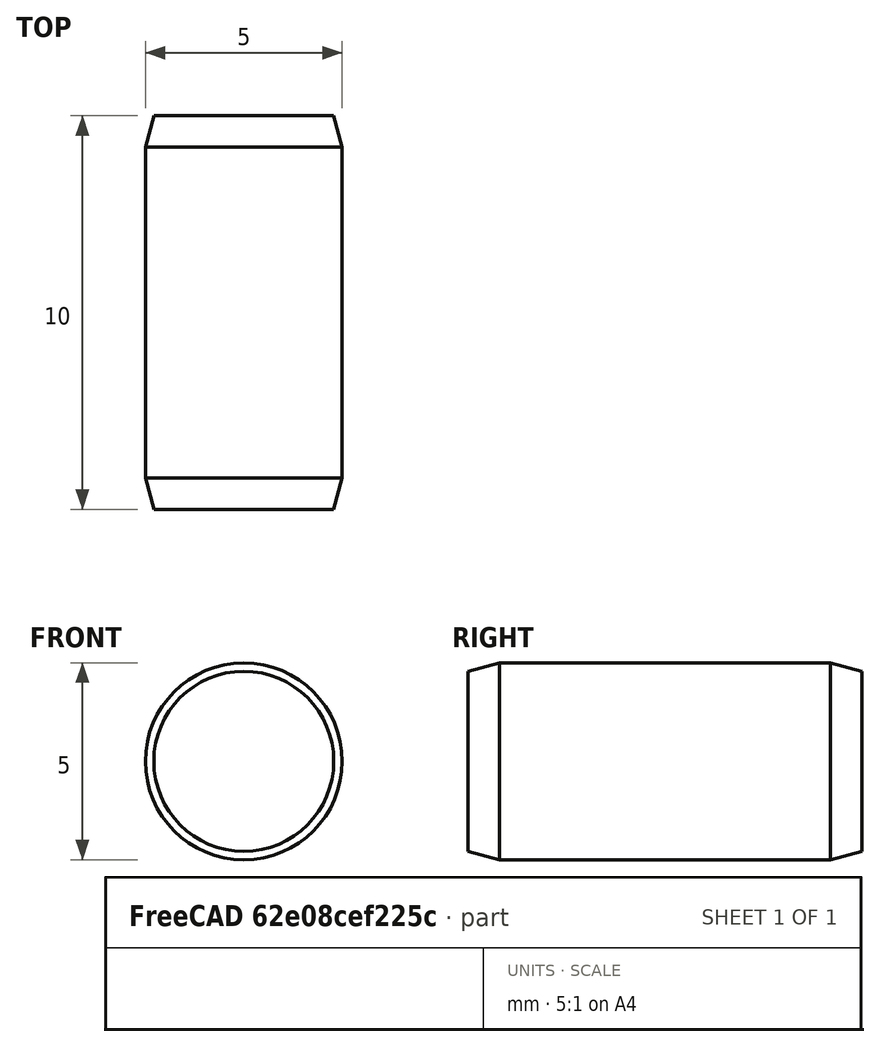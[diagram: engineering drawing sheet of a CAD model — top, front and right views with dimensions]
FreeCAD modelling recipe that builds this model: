
FCSTD DOCUMENT  (FreeCAD 0.15R4470 (Git))
Label: Zyl-Stift_ISO_8734-5x10
License: CC-BY 3.0
LicenseURL: http://creativecommons.org/licenses/by/3.0/
objects: Sketcher::SketchObject×1, PartDesign::Revolution×1
note: 3 computed .brp shape members not serialized (recipe doc carries the construction recipe); baked Part::Feature solids carry a one-line shape summary decoded from their .brp

FEATURE [Sketcher::SketchObject] Sketch
  Placement = pos=(0,0,0) rot=(0.57735,0.57735,0.57735;2.0944rad)
  sketch-geometry (7):
    g0: LineSegment StartX=0 StartY=0 StartZ=0 EndX=0 EndY=2.28564 EndZ=0
    g1: LineSegment StartX=0 StartY=2.28564 StartZ=0 EndX=0.8 EndY=2.5 EndZ=0
    g2: LineSegment StartX=0.8 StartY=2.5 StartZ=0 EndX=9.2 EndY=2.5 EndZ=0
    g3: LineSegment StartX=9.2 StartY=2.5 StartZ=0 EndX=10 EndY=2.28564 EndZ=0
    g4: LineSegment StartX=10 StartY=2.28564 StartZ=0 EndX=10 EndY=0 EndZ=0
    g5: LineSegment StartX=10 StartY=0 StartZ=0 EndX=0 EndY=0 EndZ=0
    g6: LineSegment [constr] StartX=0 StartY=2.28564 StartZ=0 EndX=10 EndY=2.28564 EndZ=0
  constraints (19):
    c: Coincident(g0,g-1)
    c: PointOnObject(g0,g-2)
    c: Coincident(g0,g1)
    c: Coincident(g1,g2)
    c: Horizontal(g2)
    c: Coincident(g2,g3)
    c: Coincident(g3,g4)
    c: Vertical(g4)
    c: Coincident(g4,g5)
    c: Coincident(g5,g-1)
    c: Horizontal(g5)
    c: Equal(g3,g1)
    c: Coincident(g6,g0)
    c: Coincident(g6,g3)
    c: Horizontal(g6)
    c: Angle(g6,g1) = 0.261799
    c: DistanceY(g-1,g1) = 2.5
    c: DistanceX(g5) = -10
    c: DistanceX(g1) = 0.8
FEATURE [PartDesign::Revolution] Revolution  label="Zyl-Stift ISO 8734-5x10 #"
  Angle = 360
  Axis = (0,1,0)
  Base = (0,0,0)
  Placement = pos=(0,0,0) rot=(0.57735,0.57735,0.57735;2.0944rad)
  ReferenceAxis = -> Sketch [H_Axis]
  Sketch = -> Sketch
